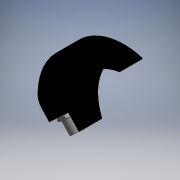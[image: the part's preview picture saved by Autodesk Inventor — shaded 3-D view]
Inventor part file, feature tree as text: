
AUTODESK INVENTOR PART (.ipt)
format: ipt  version: 2017.3 (Build 213256000, 256)  size: 322,048 bytes
history: native  units: mm (DEFAULTED — no unit token found)
features: sketch x10, other x10, revolve x7, extrude x5, hole x1
ambient origin geometry x8: Origin, YZ Plane, XZ Plane, XY Plane, X Axis, Y Axis, Z Axis, Center Point
bodies: Solid1 (feature_tree)
feature tree (33):
  extrude  "Extrusion1"  TaperAngle=360.0deg  [1 undecoded]
  revolve  "Revolution1"  [1 undecoded]
  revolve  "Revolution2"  Angle=360.0deg
  sketch  "Sketch_4"  dims[d9=1.0mm d10=6.0mm d11=4.0mm d12=2.0mm d13=90.0deg d14=9.2mm d15=0.0mm d16=360.0deg]
  sketch  "Sketch_5"  dims[d17=360.0deg d18=360.0deg]
  extrude  "Extrusion2"  TaperAngle=360.0deg  [1 undecoded]
  extrude  "Extrusion3"  TaperAngle=360.0deg  [1 undecoded]
  revolve  "Revolution3"  Angle=360.0deg
  hole  "Hole1"  [1 undecoded]
  revolve  "Revolution4"  [1 undecoded]
  revolve  "Revolution5"  [1 undecoded]
  revolve  "Revolution6"  [1 undecoded]
  extrude  "Extrusion4"  [1 undecoded]
  revolve  "Revolution7"  [1 undecoded]
  extrude  "Extrusion5"  [1 undecoded]
  other  "welle_XY"
  other  "welle_YZ"
  other  "welle_ZX"
  other  "welle_X"
  other  "welle_Y"
  other  "welle_Z"
  other  "welle_Center"
  sketch  "Sketch_1"  dims[d0=12.0mm d1=0.0mm d2=360.0deg]
  sketch  "Sketch_2"  dims[d3=360.0deg d4=1.3mm d5=0.0mm]
  sketch  "Sketch_3"  dims[d6=1.3mm d7=0.0mm d8=360.0deg]
  sketch  "Sketch_6"  dims[d19=7.6mm d20=0.0mm d21=360.0deg]
  sketch  "Sketch7"  dims[d22=2.0mm d23=0.0mm]
  other  "Flanschdosenbohrungen_Sketch_7_0"
  other  "Flanschdosenbohrungen_Sketch_7_1"
  other  "Flanschdosenbohrungen_Sketch_7_2"
  sketch  "Sketch_9"
  sketch  "Sketch_10"
  sketch  "Sketch_11"
note: 11 required parameter values undecoded (feature->parameter linkage not recoverable at this tier; creation-order binding heuristic only, values carry confidence <= 0.55)